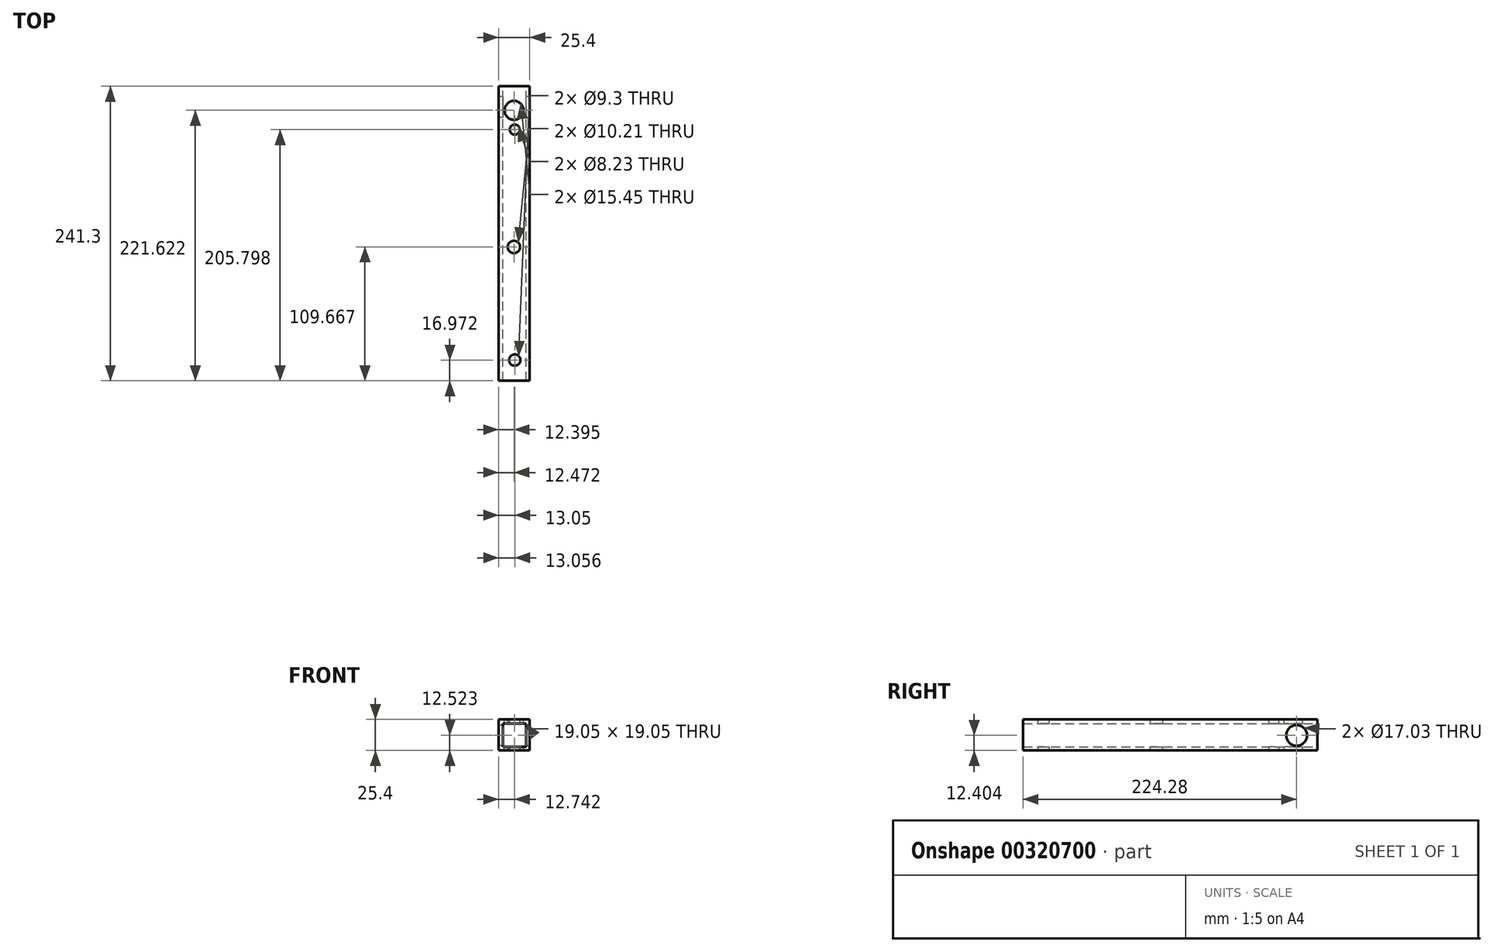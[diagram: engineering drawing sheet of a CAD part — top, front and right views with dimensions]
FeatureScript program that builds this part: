
annotation { "Feature Type Name" : "Feature", "Feature Type Description" : "" }
export const myFeature = defineFeature(function(context is Context, id is Id, definition is map)
    precondition{}
    {
        {
            var Q0;
            Q0=qCreatedBy(makeId("Top.planeOp"),FACE);
            var sketch = newSketch(context, id + "F0", { "sketchPlane" : qUnion([Q0])});
            skLineSegment(sketch, "E0", {"start": v(-46.95, 204.33) * mm, "end": v(-46.95, -36.97) * mm});
            skLineSegment(sketch, "E1", {"start": v(-46.95, -36.97) * mm, "end": v(-21.55, -36.97) * mm});
            skLineSegment(sketch, "E2", {"start": v(-21.55, -36.97) * mm, "end": v(-21.55, 204.33) * mm});
            skLineSegment(sketch, "E3", {"start": v(-21.55, 204.33) * mm, "end": v(-46.95, 204.33) * mm});
            skSolve(sketch);
        }
        {
            var Q0;
            Q0=makeQuery(id+"F0.imprint","IMPRINT",FACE,{"disambiguationData":[TD([[makeQuery(id+"F0.imprint","IMPRINT",EDGE,{"derivedFrom":sQuery(id+"F0.wireOp",EDGE,"E0")}),1.0]])]});
            extrude(context, id + "F1", {"entities" : qUnion([Q0]), "depth" : 25.4 * mm});
        }
        {
            var Q0;
            Q0=makeQuery(id+"F1.opExtrude","SWEPT_FACE",FACE,{"disambiguationData":[OSD([sQuery(id+"F0.wireOp",EDGE,"E3")])]});
            var sketch = newSketch(context, id + "F2", { "sketchPlane" : qUnion([Q0])});
            skLineSegment(sketch, "E4", {"start": v(24.68, 22.05) * mm, "end": v(24.68, 3) * mm});
            skLineSegment(sketch, "E5", {"start": v(24.68, 3) * mm, "end": v(43.73, 3) * mm});
            skLineSegment(sketch, "E6", {"start": v(43.73, 3) * mm, "end": v(43.73, 22.05) * mm});
            skLineSegment(sketch, "E7", {"start": v(43.73, 22.05) * mm, "end": v(24.68, 22.05) * mm});
            skSolve(sketch);
        }
        {
            var Q0;
            Q0=makeQuery(id+"F2.imprint","IMPRINT",FACE,{"disambiguationData":[TD([[makeQuery(id+"F2.imprint","IMPRINT",EDGE,{"derivedFrom":sQuery(id+"F2.wireOp",EDGE,"E4")}),1.0]])]});
            extrude(context, id + "F3", {"entities" : qUnion([Q0]), "operationType" : NewBodyOperationType.REMOVE, "oppositeDirection" : true, "depth" : 255.84 * mm});
        }
        {
            var Q0;
            Q0=makeQuery(id+"F1.opExtrude","CAP_FACE",FACE,{"disambiguationData":[OSD([sQuery(id+"F0.wireOp",EDGE,"E0"),sQuery(id+"F0.wireOp",EDGE,"E1"),sQuery(id+"F0.wireOp",EDGE,"E2"),sQuery(id+"F0.wireOp",EDGE,"E3")])],"isStart":false});
            var sketch = newSketch(context, id + "F4", { "sketchPlane" : qUnion([Q0])});
            skCircle(sketch, "E8", {"center": v(-34.48, 184.65) * mm, "radius": 7.73 * mm});
            skCircle(sketch, "E9", {"center": v(-33.9, 168.83) * mm, "radius": 4.12 * mm});
            skCircle(sketch, "E10", {"center": v(-34.55, 72.7) * mm, "radius": 5.1 * mm});
            skSolve(sketch);
        }
        {
            var Q0;
            Q0=makeQuery(id+"F4.imprint","IMPRINT",FACE,{"disambiguationData":[TD([[makeQuery(id+"F4.imprint","IMPRINT",EDGE,{"derivedFrom":sQuery(id+"F4.wireOp",EDGE,"E8")}),-1.0]])]});
            var sketch = newSketch(context, id + "F5", { "sketchPlane" : qUnion([Q0]), "disableImprinting" : false});
            skCircle(sketch, "E11", {"center": v(-33.9, -20) * mm, "radius": 4.65 * mm});
            skCircle(sketch, "E12", {"center": v(-37.1, 117.14) * mm, "radius": 7.09 * mm});
            skSolve(sketch);
        }
        {
            var Q0;
            Q0=makeQuery(id+"F4.imprint","IMPRINT",FACE,{"disambiguationData":[TD([[makeQuery(id+"F4.imprint","IMPRINT",EDGE,{"derivedFrom":sQuery(id+"F4.wireOp",EDGE,"E8")}),1.0]])]});
            var Q1;
            Q1=makeQuery(id+"F4.imprint","IMPRINT",FACE,{"disambiguationData":[TD([[makeQuery(id+"F4.imprint","IMPRINT",EDGE,{"derivedFrom":sQuery(id+"F4.wireOp",EDGE,"E9")}),1.0]])]});
            var Q2;
            Q2=makeQuery(id+"F4.imprint","IMPRINT",FACE,{"disambiguationData":[TD([[makeQuery(id+"F4.imprint","IMPRINT",EDGE,{"derivedFrom":sQuery(id+"F4.wireOp",EDGE,"E10")}),1.0]])]});
            var Q3;
            Q3=makeQuery(id+"F5.imprint","IMPRINT",FACE,{"disambiguationData":[TD([[makeQuery(id+"F5.imprint","IMPRINT",EDGE,{"derivedFrom":sQuery(id+"F5.wireOp",EDGE,"E11")}),1.0]])]});
            extrude(context, id + "F6", {"entities" : qUnion([Q0, Q1, Q2, Q3]), "operationType" : NewBodyOperationType.REMOVE, "oppositeDirection" : true, "depth" : 73.48 * mm});
        }
        {
            var Q0;
            Q0=makeQuery(id+"F1.opExtrude","SWEPT_FACE",FACE,{"disambiguationData":[OSD([sQuery(id+"F0.wireOp",EDGE,"E0")])]});
            var sketch = newSketch(context, id + "F7", { "sketchPlane" : qUnion([Q0])});
            skCircle(sketch, "E13", {"center": v(-187.31, 12.4) * mm, "radius": 8.51 * mm});
            skSolve(sketch);
        }
        {
            var Q0;
            Q0=qSketchRegion(id+"F7",true);
            extrude(context, id + "F8", {"entities" : qUnion([Q0]), "operationType" : NewBodyOperationType.REMOVE, "oppositeDirection" : true, "depth" : 25.4 * mm});
        }
    });
